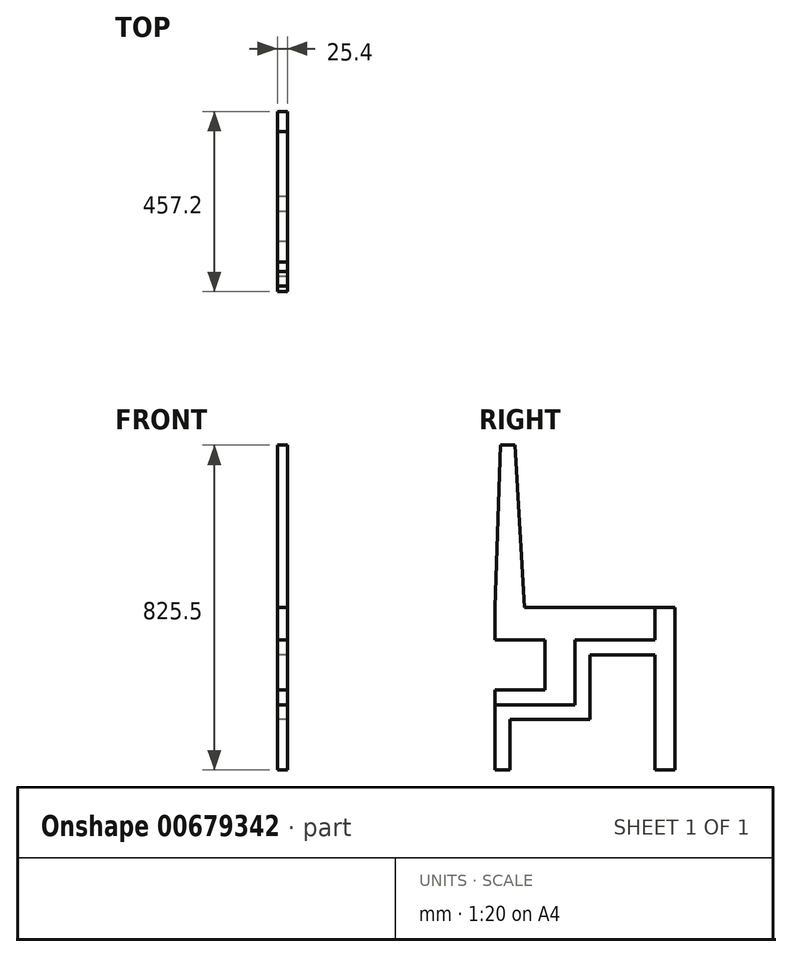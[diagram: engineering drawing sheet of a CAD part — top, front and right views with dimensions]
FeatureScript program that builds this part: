
annotation { "Feature Type Name" : "Feature", "Feature Type Description" : "" }
export const myFeature = defineFeature(function(context is Context, id is Id, definition is map)
    precondition{}
    {
        {
            var Q0;
            Q0=qCreatedBy(makeId("Right.planeOp"),FACE);
            var sketch = newSketch(context, id + "F0", { "sketchPlane" : qUnion([Q0])});
            skLineSegment(sketch, "E0", {"start": v(0, 0) * mm, "end": v(0, 165.1) * mm});
            skLineSegment(sketch, "E1", {"start": v(203.2, 165.1) * mm, "end": v(0, 165.1) * mm});
            skLineSegment(sketch, "E2", {"start": v(203.2, 165.1) * mm, "end": v(203.2, 330.2) * mm});
            skLineSegment(sketch, "E3", {"start": v(203.2, 330.2) * mm, "end": v(406.4, 330.2) * mm});
            skLineSegment(sketch, "E4", {"start": v(612.73, 412.75) * mm, "end": v(612.73, 0) * mm, "construction": true});
            skLineSegment(sketch, "E5", {"start": v(203.2, 330.2) * mm, "end": v(-965.57, 330.2) * mm, "construction": true});
            skLineSegment(sketch, "E6", {"start": v(406.4, 330.2) * mm, "end": v(406.4, 0) * mm});
            skLineSegment(sketch, "E7", {"start": v(0, 165.1) * mm, "end": v(-965.57, 165.1) * mm, "construction": true});
            skLineSegment(sketch, "E8", {"start": v(406.4, 0) * mm, "end": v(0, 0) * mm});
            skLineSegment(sketch, "E9", {"start": v(612.73, 0) * mm, "end": v(406.4, 0) * mm, "construction": true});
            skLineSegment(sketch, "E10", {"start": v(406.4, 330.2) * mm, "end": v(406.4, 412.75) * mm});
            skLineSegment(sketch, "E11", {"start": v(406.4, 412.75) * mm, "end": v(0, 412.75) * mm});
            skLineSegment(sketch, "E12", {"start": v(0, 412.75) * mm, "end": v(0, 165.1) * mm});
            skLineSegment(sketch, "E13", {"start": v(406.4, 412.75) * mm, "end": v(612.73, 412.75) * mm, "construction": true});
            skLineSegment(sketch, "E14", {"start": v(0, 412.75) * mm, "end": v(0, 825.5) * mm});
            skLineSegment(sketch, "E15", {"start": v(203.2, 330.2) * mm, "end": v(203.2, 515.87) * mm, "construction": true});
            skLineSegment(sketch, "E16", {"start": v(203.2, 515.87) * mm, "end": v(-40.5, 515.87) * mm, "construction": true});
            skLineSegment(sketch, "E17", {"start": v(-40.5, 515.87) * mm, "end": v(-40.5, 165.1) * mm, "construction": true});
            skLineSegment(sketch, "E18", {"start": v(-40.5, 165.1) * mm, "end": v(0, 165.1) * mm});
            skLineSegment(sketch, "E19", {"start": v(406.4, 0) * mm, "end": v(457.2, 0) * mm});
            skLineSegment(sketch, "E20", {"start": v(457.2, 412.75) * mm, "end": v(406.4, 412.75) * mm});
            skLineSegment(sketch, "E21", {"start": v(0, 825.5) * mm, "end": v(50.8, 825.5) * mm});
            skLineSegment(sketch, "E22", {"start": v(50.8, 825.5) * mm, "end": v(50.8, 412.75) * mm});
            skLineSegment(sketch, "E23", {"start": v(457.2, 412.75) * mm, "end": v(457.2, 0) * mm});
            skLineSegment(sketch, "E24.bottom", {"start": v(0, 203.2) * mm, "end": v(127, 203.2) * mm});
            skLineSegment(sketch, "E24.top", {"start": v(0, 330.2) * mm, "end": v(127, 330.2) * mm});
            skLineSegment(sketch, "E24.left", {"start": v(0, 203.2) * mm, "end": v(0, 330.2) * mm});
            skLineSegment(sketch, "E24.right", {"start": v(127, 203.2) * mm, "end": v(127, 330.2) * mm});
            skLineSegment(sketch, "E25.bottom", {"start": v(241.94, 0) * mm, "end": v(406.4, 0) * mm});
            skLineSegment(sketch, "E25.top", {"start": v(241.94, 292.1) * mm, "end": v(406.4, 292.1) * mm});
            skLineSegment(sketch, "E25.left", {"start": v(241.94, 0) * mm, "end": v(241.94, 292.1) * mm});
            skLineSegment(sketch, "E25.right", {"start": v(406.4, 0) * mm, "end": v(406.4, 292.1) * mm});
            skLineSegment(sketch, "E26.bottom", {"start": v(38.04, 0) * mm, "end": v(203.2, 0) * mm});
            skLineSegment(sketch, "E26.top", {"start": v(38.04, 128.87) * mm, "end": v(203.2, 128.87) * mm});
            skLineSegment(sketch, "E26.left", {"start": v(38.04, 0) * mm, "end": v(38.04, 128.87) * mm});
            skLineSegment(sketch, "E26.right", {"start": v(203.2, 0) * mm, "end": v(203.2, 128.87) * mm});
            skLineSegment(sketch, "E27", {"start": v(50.8, 825.5) * mm, "end": v(74.6, 412.75) * mm});
            skLineSegment(sketch, "E28", {"start": v(0, 412.75) * mm, "end": v(14.48, 825.5) * mm});
            skLineSegment(sketch, "E29", {"start": v(203.2, 128.87) * mm, "end": v(241.94, 128.87) * mm});
            skSolve(sketch);
        }
        {
            var Q0;
            {var subQ9=sQuery(id+"F0.wireOp",EDGE,"E1");Q0=makeQuery(id+"F0.imprint","IMPRINT",FACE,{"disambiguationData":[TD([[makeQuery(id+"F0.imprint","IMPRINT",EDGE,{"derivedFrom":subQ9}),-1.0]])]});}
            var Q1;
            {var subQ0=sQuery(id+"F0.wireOp",EDGE,"E22");Q1=makeQuery(id+"F0.imprint","IMPRINT",FACE,{"disambiguationData":[TD([[makeQuery(id+"F0.imprint","IMPRINT",EDGE,{"derivedFrom":subQ0}),1.0]])]});}
            var Q2;
            {var subQ2=sQuery(id+"F0.wireOp",EDGE,"E22");Q2=makeQuery(id+"F0.imprint","IMPRINT",FACE,{"disambiguationData":[TD([[makeQuery(id+"F0.imprint","IMPRINT",EDGE,{"derivedFrom":subQ2}),-1.0]])]});}
            extrude(context, id + "F1", {"entities" : qUnion([Q0, Q1, Q2]), "depth" : 25.4 * mm, "offsetDistance" : 25.4 * mm});
        }
        {
            var Q0;
            Q0=makeQuery(id+"F0.imprint","IMPRINT",FACE,{"disambiguationData":[TD([[makeQuery(id+"F0.imprint","IMPRINT",EDGE,{"derivedFrom":sQuery(id+"F0.wireOp",EDGE,"E6")}),1.0]])]});
            var Q1;
            Q1=makeQuery(id+"F0.imprint","IMPRINT",FACE,{"disambiguationData":[TD([[makeQuery(id+"F0.imprint","IMPRINT",EDGE,{"derivedFrom":sQuery(id+"F0.wireOp",EDGE,"E0")}),-1.0]])]});
            extrude(context, id + "F2", {"entities" : qUnion([Q0, Q1]), "depth" : 25.4 * mm, "offsetDistance" : 25.4 * mm});
        }
    });
